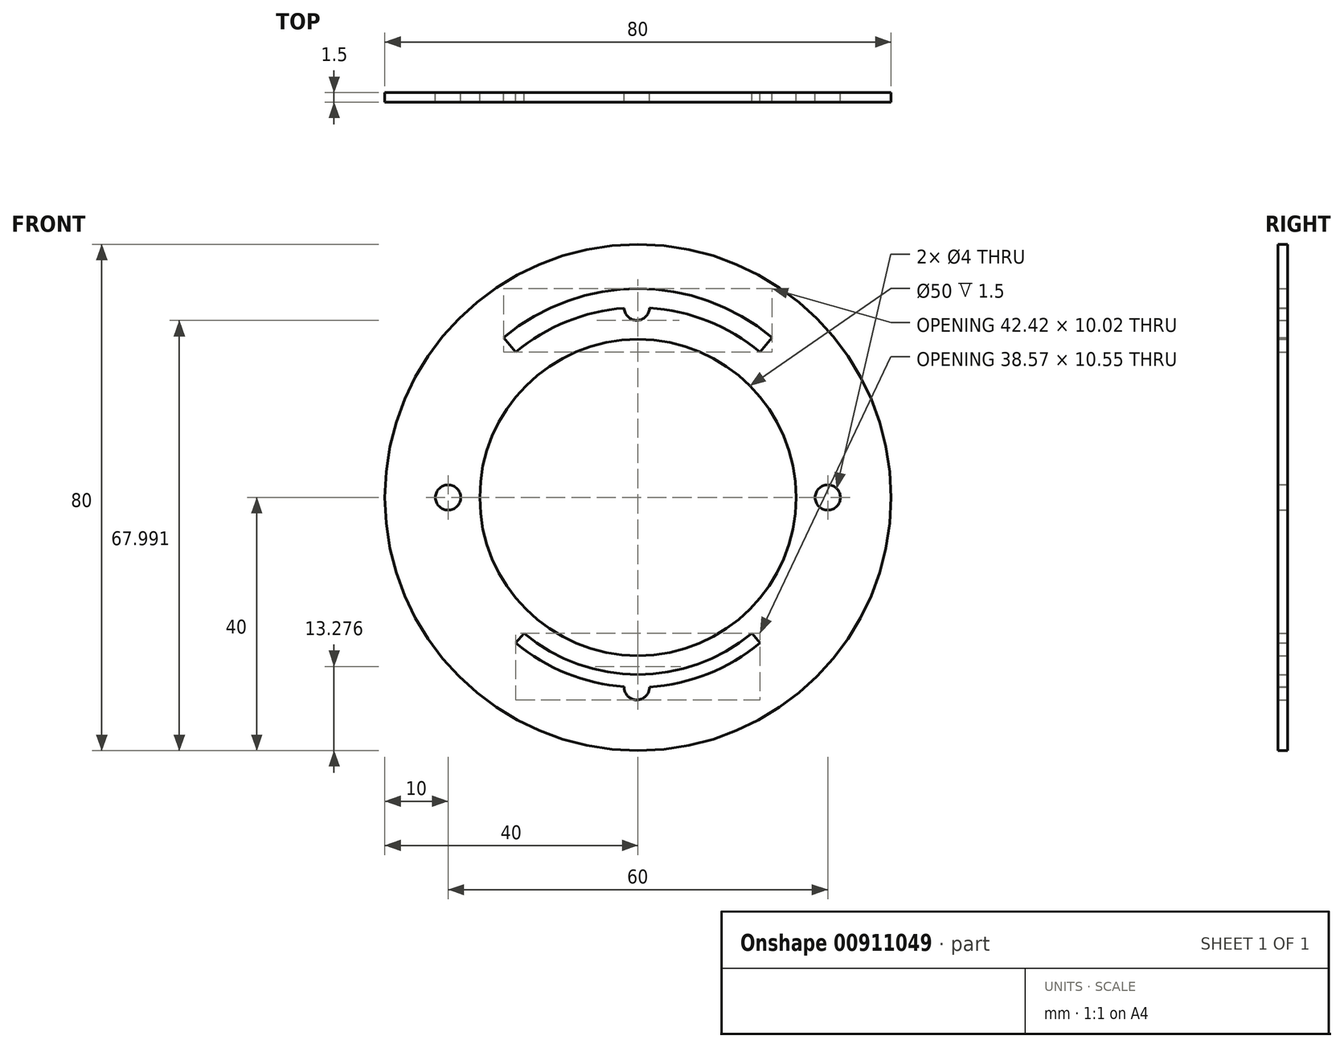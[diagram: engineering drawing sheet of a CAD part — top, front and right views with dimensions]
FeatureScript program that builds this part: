
annotation { "Feature Type Name" : "Feature", "Feature Type Description" : "" }
export const myFeature = defineFeature(function(context is Context, id is Id, definition is map)
    precondition{}
    {
        {
            var Q0;
            Q0=qCreatedBy(makeId("Front.planeOp"),FACE);
            var sketch = newSketch(context, id + "F0", { "sketchPlane" : qUnion([Q0])});
            skCircle(sketch, "E0", {"center": v(0, 0) * mm, "radius": 40 * mm});
            skArc(sketch, "E1", {"start": v(-2.18, 29.92) * mm, "mid": v(-0.17, 28) * mm, "end": v(1.82, 29.94) * mm});
            skLineSegment(sketch, "E2.MirrorCS", {"start": v(-19.28, 22.98) * mm, "end": v(-21.21, 25.28) * mm});
            skLineSegment(sketch, "E3.MirrorCS", {"start": v(19.28, 22.98) * mm, "end": v(21.21, 25.28) * mm});
            skArc(sketch, "E4.trimOffspring", {"start": v(21.21, 25.28) * mm, "mid": v(0, 33) * mm, "end": v(-21.21, 25.28) * mm});
            skArc(sketch, "E5.trimOffspring", {"start": v(19.28, 22.98) * mm, "mid": v(11.11, 27.87) * mm, "end": v(1.82, 29.94) * mm});
            skCircle(sketch, "E6", {"center": v(0, 0) * mm, "radius": 25 * mm});
            skArc(sketch, "E7.trimOffspring", {"start": v(-2.18, 29.92) * mm, "mid": v(-11.28, 27.8) * mm, "end": v(-19.28, 22.98) * mm});
            skCircle(sketch, "E8", {"center": v(-30, 0) * mm, "radius": 2 * mm});
            skCircle(sketch, "E9", {"center": v(30, 0) * mm, "radius": 2 * mm});
            skArc(sketch, "E10", {"start": v(-2.18, -29.92) * mm, "mid": v(-0.2, -32) * mm, "end": v(1.82, -29.94) * mm});
            skArc(sketch, "E11", {"start": v(-19.28, -22.98) * mm, "mid": v(-11.28, -27.8) * mm, "end": v(-2.18, -29.92) * mm});
            skArc(sketch, "E12", {"start": v(-18, -21.45) * mm, "mid": v(0, -28) * mm, "end": v(18, -21.45) * mm});
            skLineSegment(sketch, "E13", {"start": v(-18, -21.45) * mm, "end": v(-19.28, -22.98) * mm});
            skLineSegment(sketch, "E14", {"start": v(18, -21.45) * mm, "end": v(19.28, -22.98) * mm});
            skArc(sketch, "E15.trimOffspring", {"start": v(1.82, -29.94) * mm, "mid": v(11.11, -27.87) * mm, "end": v(19.28, -22.98) * mm});
            skSolve(sketch);
        }
        {
            var Q0;
            Q0 = qSketchRegion(id + "F0", true);
            extrude(context, id + "F1", {"entities" : qUnion([Q0]), "depth" : 1.5 * mm, "offsetDistance" : 25 * mm});
        }
    });
